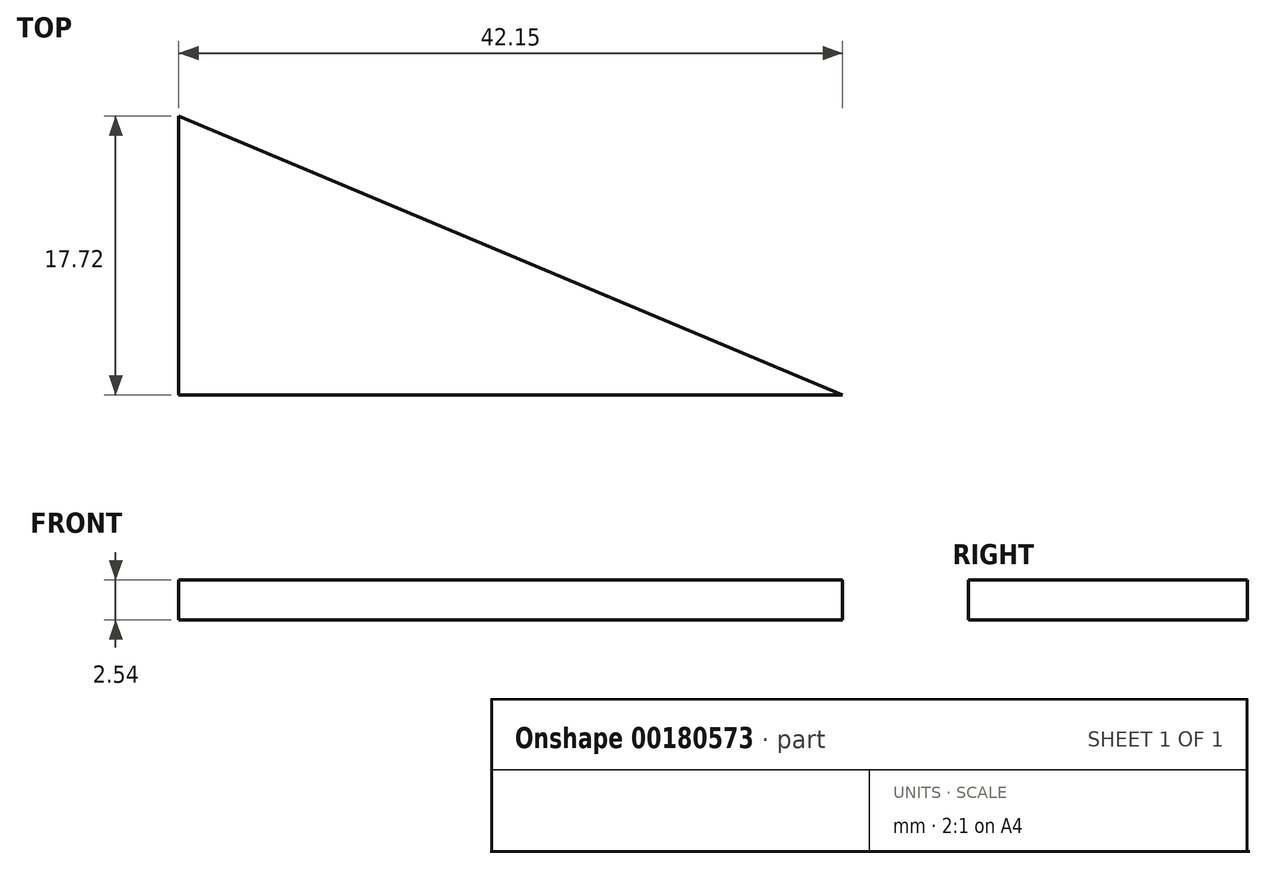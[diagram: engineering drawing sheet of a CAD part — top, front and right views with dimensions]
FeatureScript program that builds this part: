
annotation { "Feature Type Name" : "Feature", "Feature Type Description" : "" }
export const myFeature = defineFeature(function(context is Context, id is Id, definition is map)
    precondition{}
    {
        {
            var Q0;
            Q0=qCreatedBy(makeId("Top.planeOp"),FACE);
            var sketch = newSketch(context, id + "F0", { "sketchPlane" : qUnion([Q0])});
            skLineSegment(sketch, "E0", {"start": v(0, 0) * mm, "end": v(0, 17.72) * mm});
            skLineSegment(sketch, "E1", {"start": v(0, 17.72) * mm, "end": v(42.15, 0) * mm});
            skLineSegment(sketch, "E2", {"start": v(42.15, 0) * mm, "end": v(0, 0) * mm});
            skSolve(sketch);
        }
        {
            var Q0;
            Q0 = qSketchRegion(id + "F0", true);
            extrude(context, id + "F1", {"entities" : qUnion([Q0]), "depth" : 2.54 * mm});
        }
    });
